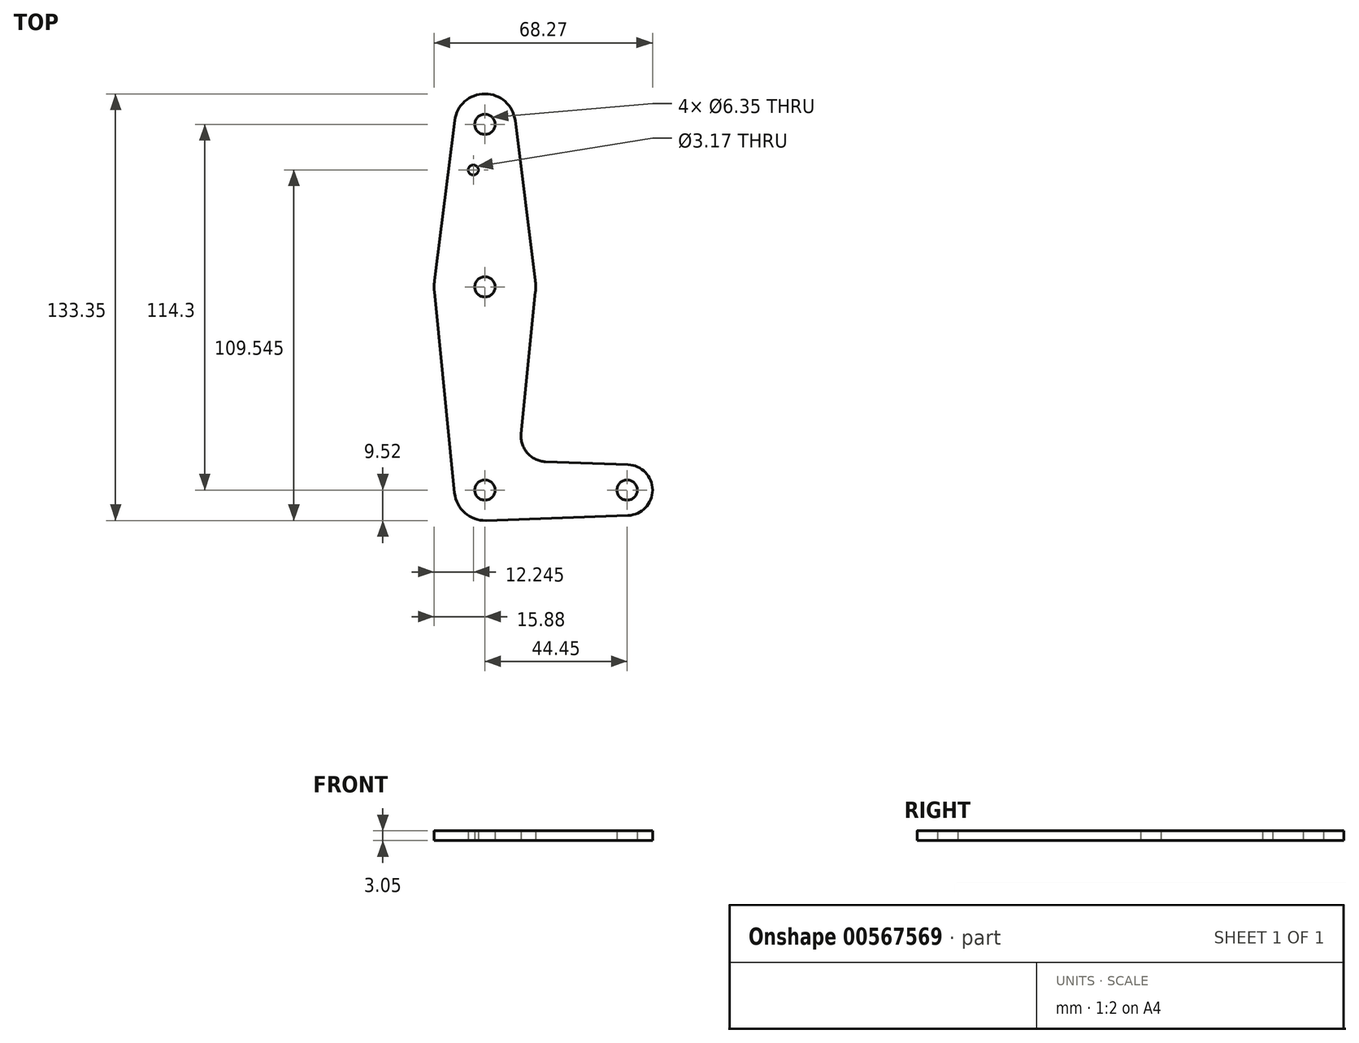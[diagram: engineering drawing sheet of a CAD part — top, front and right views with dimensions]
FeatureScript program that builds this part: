
annotation { "Feature Type Name" : "Feature", "Feature Type Description" : "" }
export const myFeature = defineFeature(function(context is Context, id is Id, definition is map)
    precondition{}
    {
        {
            var Q0;
            Q0=qCreatedBy(makeId("Top.planeOp"),FACE);
            var sketch = newSketch(context, id + "F0", { "sketchPlane" : qUnion([Q0])});
            skLineSegment(sketch, "E0", {"start": v(0, 0) * mm, "end": v(0, 63.5) * mm});
            skLineSegment(sketch, "E1", {"start": v(0, 63.5) * mm, "end": v(0, 114.3) * mm});
            skLineSegment(sketch, "E2", {"start": v(0, 0) * mm, "end": v(44.45, 0) * mm});
            skCircle(sketch, "E3", {"center": v(0, 0) * mm, "radius": 9.53 * mm});
            skCircle(sketch, "E4", {"center": v(0, 63.5) * mm, "radius": 15.88 * mm});
            skCircle(sketch, "E5", {"center": v(0, 114.3) * mm, "radius": 9.53 * mm});
            skCircle(sketch, "E6", {"center": v(44.45, 0) * mm, "radius": 7.94 * mm});
            skLineSegment(sketch, "E7", {"start": v(-9.45, 115.5) * mm, "end": v(-15.75, 65.48) * mm});
            skLineSegment(sketch, "E8", {"start": v(9.44, 115.54) * mm, "end": v(15.75, 65.48) * mm});
            skLineSegment(sketch, "E9", {"start": v(18.97, 8.85) * mm, "end": v(44.73, 7.93) * mm});
            skLineSegment(sketch, "E10", {"start": v(44.73, 7.93) * mm, "end": v(44.73, -7.93) * mm});
            skLineSegment(sketch, "E11", {"start": v(44.73, -7.93) * mm, "end": v(0, -9.53) * mm});
            skLineSegment(sketch, "E12", {"start": v(15.8, 61.91) * mm, "end": v(11.34, 17.6) * mm});
            skCircle(sketch, "E13", {"center": v(44.45, 0) * mm, "radius": 3.18 * mm});
            skCircle(sketch, "E14", {"center": v(0, 0) * mm, "radius": 3.18 * mm});
            skPoint(sketch, "E15.newPointB", {"position": v(0, 9.53) * mm});
            skArc(sketch, "E15.filletArc", {"start": v(11.34, 17.6) * mm, "mid": v(13.26, 11.57) * mm, "end": v(18.97, 8.85) * mm});
            skLineSegment(sketch, "E16", {"start": v(-15.8, 61.91) * mm, "end": v(-9.48, -0.95) * mm});
            skCircle(sketch, "E17", {"center": v(0, 63.5) * mm, "radius": 3.18 * mm});
            skCircle(sketch, "E18", {"center": v(0, 114.3) * mm, "radius": 3.18 * mm});
            skCircle(sketch, "E19", {"center": v(-3.63, 100.03) * mm, "radius": 1.59 * mm});
            skSolve(sketch);
        }
        {
            var Q0;
            Q0 = qSketchRegion(id + "F0", true);
            var Q1;
            {var subQ0=sQuery(id+"F0.wireOp",EDGE,"E14");var subQ1=sQuery(id+"F0.wireOp",EDGE,"E0");var subQ2=makeQuery(id+"F0.imprint","INTERSECT",VERTEX,{"derivedFrom":[subQ1,subQ0]});Q1=makeQuery(id+"F0.imprint","IMPRINT",FACE,{"disambiguationData":[TD([[makeQuery(id+"F0.imprint","IMPRINT",EDGE,{"disambiguationData":[TD([[subQ2,-1.0]])],"derivedFrom":subQ1}),-1.0]])]});}
            extrude(context, id + "F1", {"entities" : qUnion([Q0, Q1]), "depth" : 3.05 * mm, "offsetDistance" : 25.4 * mm});
        }
    });
